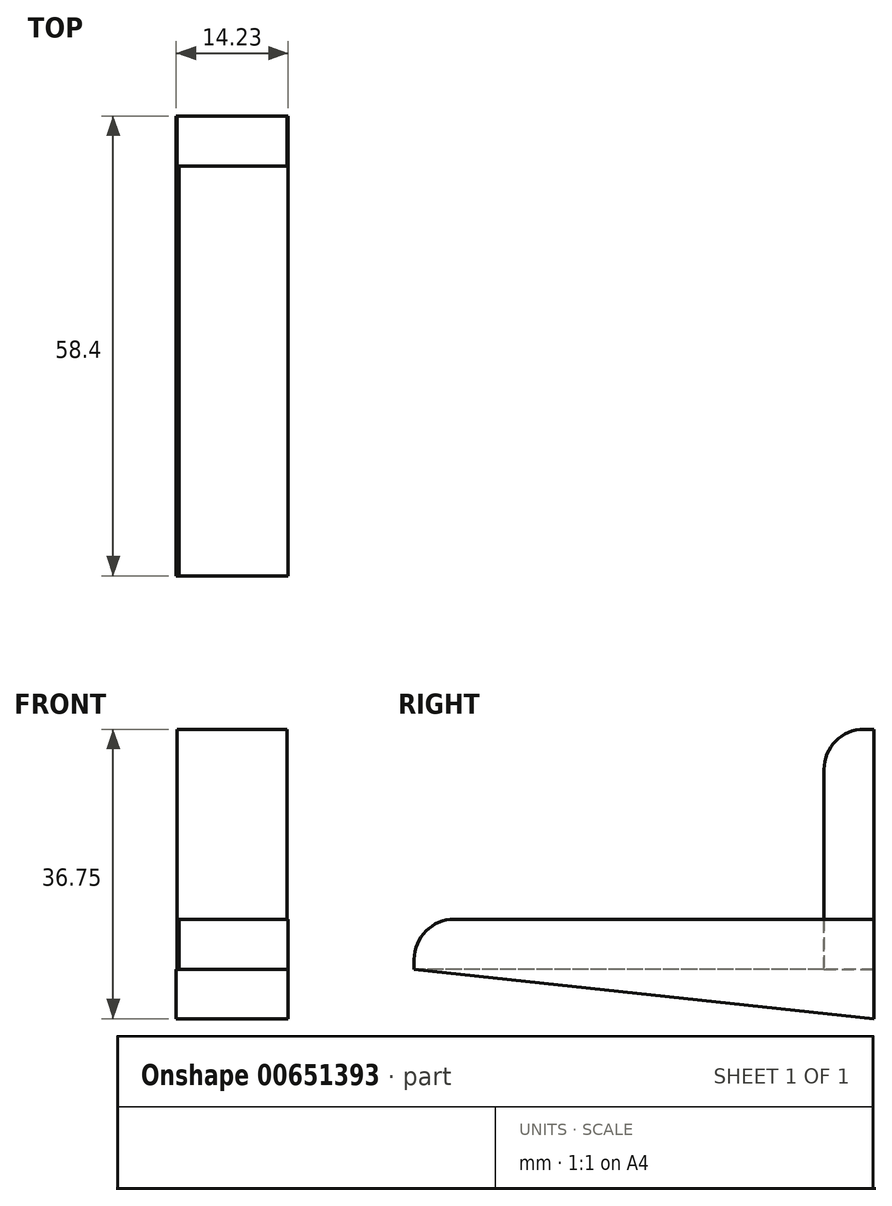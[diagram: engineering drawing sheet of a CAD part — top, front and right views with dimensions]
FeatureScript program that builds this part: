
annotation { "Feature Type Name" : "Feature", "Feature Type Description" : "" }
export const myFeature = defineFeature(function(context is Context, id is Id, definition is map)
    precondition{}
    {
        {
            var Q0;
            Q0=qCreatedBy(makeId("Front.planeOp"),FACE);
            var sketch = newSketch(context, id + "F0", { "sketchPlane" : qUnion([Q0])});
            skLineSegment(sketch, "E0.bottom", {"start": v(-22.54, 0) * mm, "end": v(-8.57, 0) * mm});
            skLineSegment(sketch, "E0.top", {"start": v(-22.54, 30.48) * mm, "end": v(-8.57, 30.48) * mm});
            skLineSegment(sketch, "E0.left", {"start": v(-22.54, 0) * mm, "end": v(-22.54, 30.48) * mm});
            skLineSegment(sketch, "E0.right", {"start": v(-8.57, 0) * mm, "end": v(-8.57, 30.48) * mm});
            skSolve(sketch);
        }
        {
            var Q0;
            Q0=qCreatedBy(makeId("Top.planeOp"),FACE);
            var sketch = newSketch(context, id + "F1", { "sketchPlane" : qUnion([Q0])});
            skLineSegment(sketch, "E1.bottom", {"start": v(-22.27, 0) * mm, "end": v(-8.41, 0) * mm});
            skLineSegment(sketch, "E1.top", {"start": v(-22.27, -58.4) * mm, "end": v(-8.41, -58.4) * mm});
            skLineSegment(sketch, "E1.left", {"start": v(-22.27, 0) * mm, "end": v(-22.27, -58.4) * mm});
            skLineSegment(sketch, "E1.right", {"start": v(-8.41, 0) * mm, "end": v(-8.41, -58.4) * mm});
            skSolve(sketch);
        }
        {
            var Q0;
            Q0 = qSketchRegion(id + "F1", true);
            extrude(context, id + "F2", {"entities" : qUnion([Q0]), "depth" : 6.35 * mm, "offsetDistance" : 25.4 * mm});
        }
        {
            var Q0;
            Q0=makeQuery(id+"F0.imprint","IMPRINT",FACE,{"disambiguationData":[TD([[makeQuery(id+"F0.imprint","IMPRINT",EDGE,{"derivedFrom":sQuery(id+"F0.wireOp",EDGE,"E0.bottom")}),1.0]])]});
            extrude(context, id + "F3", {"entities" : qUnion([Q0]), "operationType" : NewBodyOperationType.ADD, "depth" : 6.35 * mm, "offsetDistance" : 25.4 * mm});
        }
        {
            var Q0;
            Q0=makeQuery(id+"F2.opExtrude","CAP_EDGE",EDGE,{"disambiguationData":[OSD([sQuery(id+"F1.wireOp",EDGE,"E1.top")])],"isStart":false});
            var Q1;
            Q1=makeQuery(id+"F3.opExtrude","CAP_EDGE",EDGE,{"disambiguationData":[OSD([sQuery(id+"F0.wireOp",EDGE,"E0.top")])],"isStart":false});
            fillet(context, id + "F4", {"entities" : qUnion([Q0, Q1]), "radius" : 5.08 * mm, "tangentPropagation" : true, "allowEdgeOverflow" : false});
        }
        {
            var Q0;
            Q0=makeQuery(id+"F2.opExtrude","SWEPT_FACE",FACE,{"disambiguationData":[OSD([sQuery(id+"F1.wireOp",EDGE,"E1.right")])]});
            var sketch = newSketch(context, id + "F5", { "sketchPlane" : qUnion([Q0])});
            skLineSegment(sketch, "E2", {"start": v(-58.4, 0) * mm, "end": v(0, -6.27) * mm});
            skLineSegment(sketch, "E3", {"start": v(0, -6.27) * mm, "end": v(0, 0) * mm});
            skSolve(sketch);
        }
        {
            var Q0;
            Q0=makeQuery(id+"F5.imprint","IMPRINT",FACE,{"disambiguationData":[TD([[makeQuery(id+"F5.imprint","IMPRINT",EDGE,{"derivedFrom":sQuery(id+"F5.wireOp",EDGE,"E2")}),1.0]])]});
            extrude(context, id + "F6", {"entities" : qUnion([Q0]), "operationType" : NewBodyOperationType.ADD, "oppositeDirection" : true, "depth" : 14.22 * mm, "offsetDistance" : 25.4 * mm});
        }
    });
